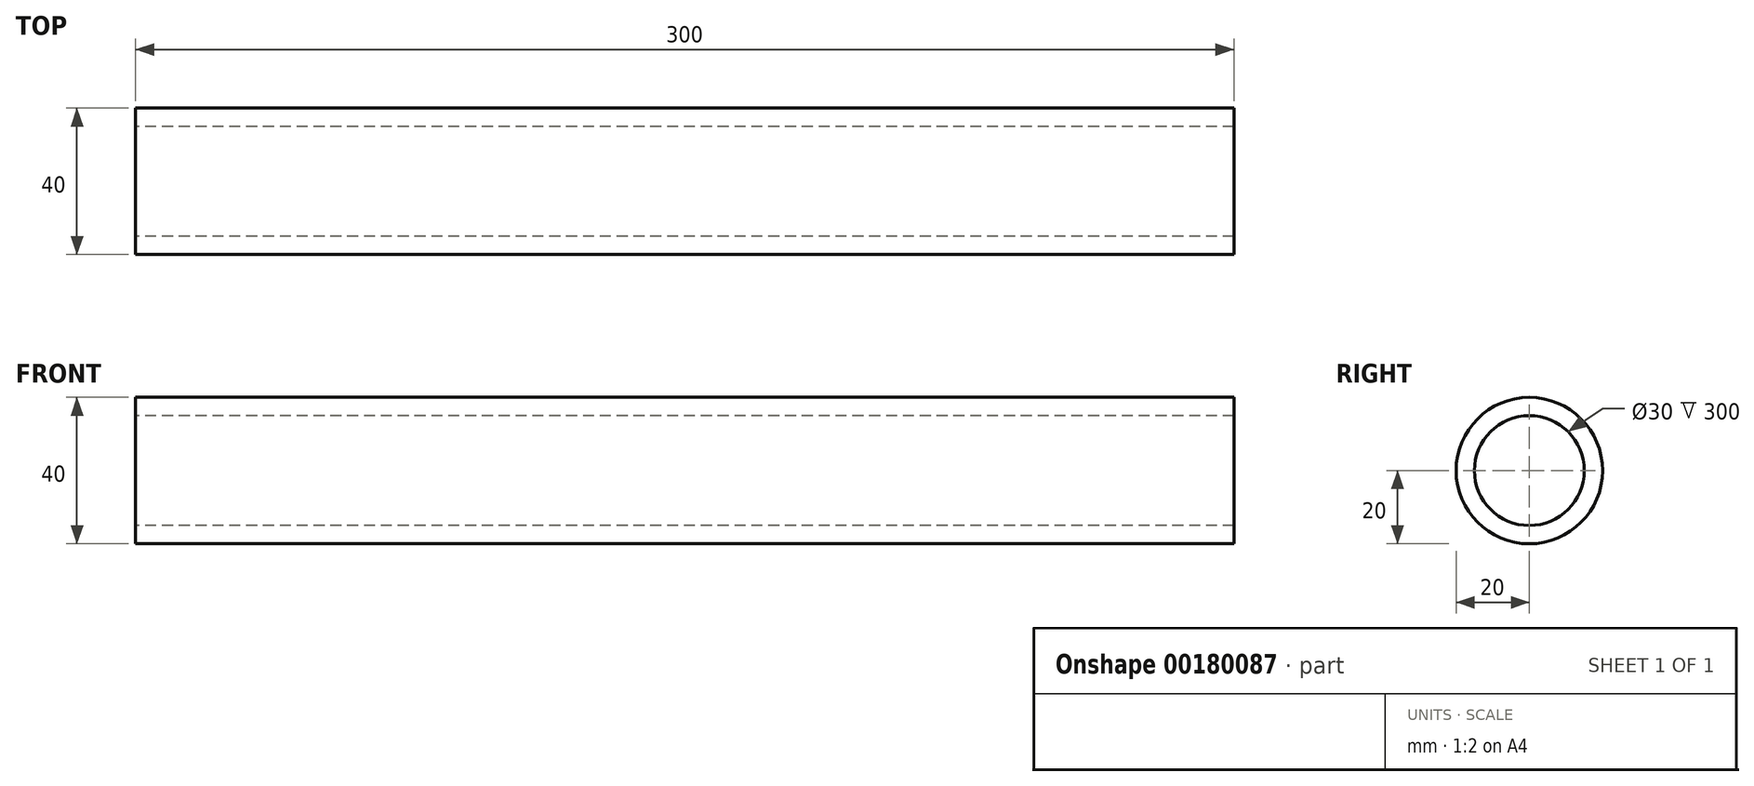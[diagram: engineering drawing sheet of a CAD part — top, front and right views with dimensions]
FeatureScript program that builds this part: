
annotation { "Feature Type Name" : "Feature", "Feature Type Description" : "" }
export const myFeature = defineFeature(function(context is Context, id is Id, definition is map)
    precondition{}
    {
        {
            var Q0;
            Q0=qCreatedBy(makeId("Right.planeOp"),FACE);
            var sketch = newSketch(context, id + "F0", { "sketchPlane" : qUnion([Q0])});
            skCircle(sketch, "E0", {"center": v(0, 0) * mm, "radius": 20 * mm});
            skCircle(sketch, "E1", {"center": v(0, 0) * mm, "radius": 15 * mm});
            skSolve(sketch);
        }
        {
            var Q0;
            Q0=makeQuery(id+"F0.imprint","IMPRINT",FACE,{"disambiguationData":[TD([[makeQuery(id+"F0.imprint","IMPRINT",EDGE,{"derivedFrom":sQuery(id+"F0.wireOp",EDGE,"E0")}),1.0]])]});
            extrude(context, id + "F1", {"entities" : qUnion([Q0]), "depth" : 300 * mm});
        }
    });
